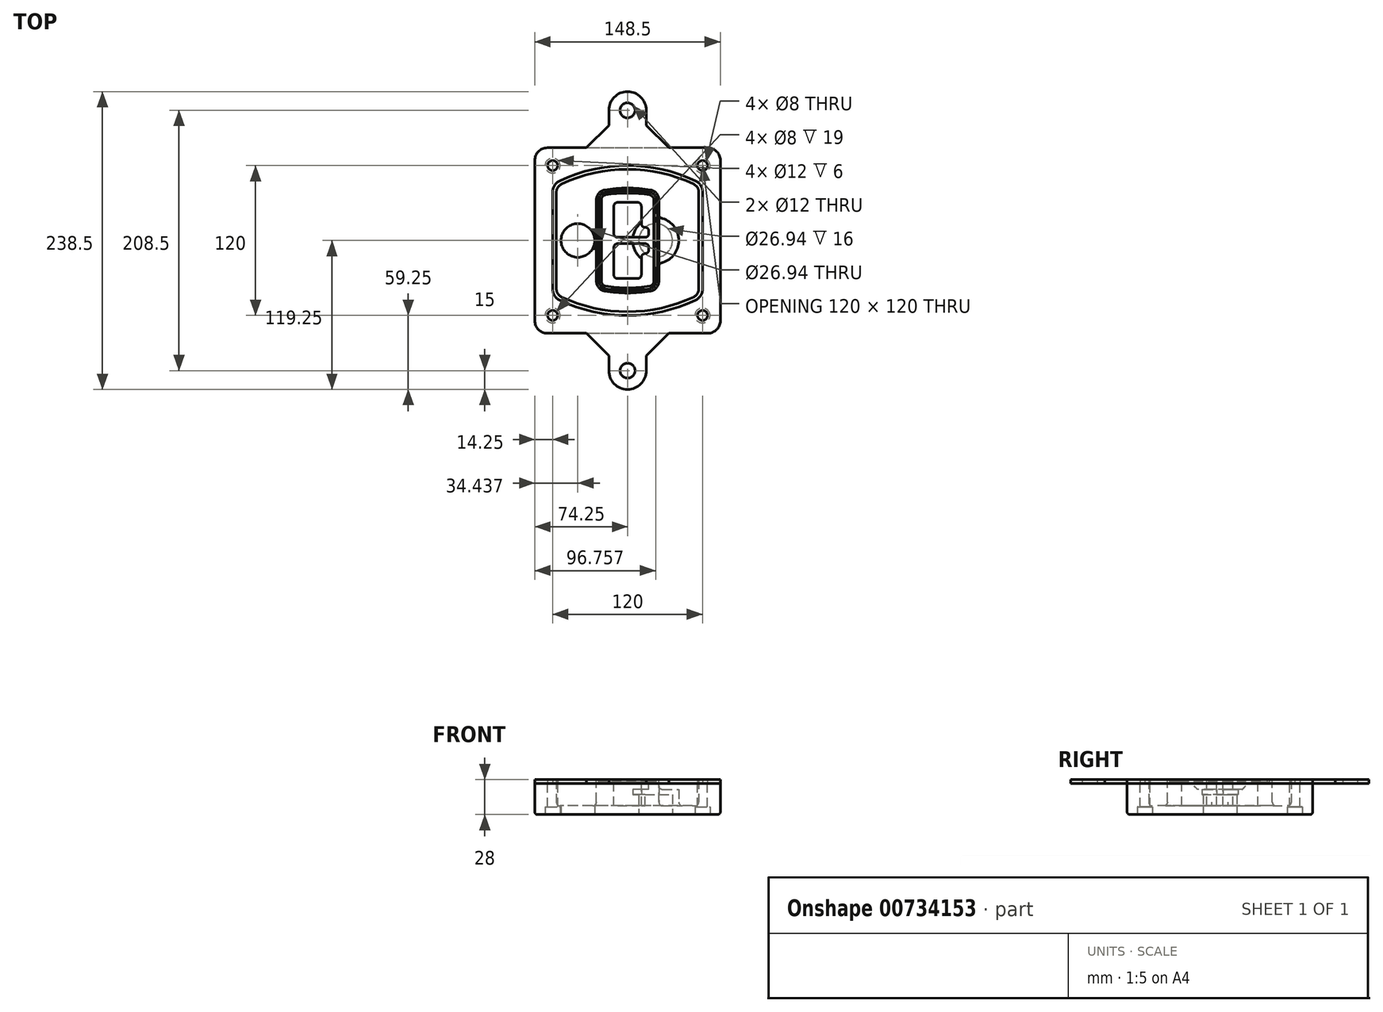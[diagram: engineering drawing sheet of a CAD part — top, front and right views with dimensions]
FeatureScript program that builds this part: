
annotation { "Feature Type Name" : "Feature", "Feature Type Description" : "" }
export const myFeature = defineFeature(function(context is Context, id is Id, definition is map)
    precondition{}
    {
        {
            var Q0;
            Q0=qCreatedBy(makeId("Top.planeOp"),FACE);
            var sketch = newSketch(context, id + "F0", { "sketchPlane" : qUnion([Q0])});
            skPoint(sketch, "E0.rect.middle", {"position": v(0, 0) * mm});
            skLineSegment(sketch, "E1.bottom", {"start": v(-64.25, -74.25) * mm, "end": v(64.25, -74.25) * mm});
            skLineSegment(sketch, "E1.top", {"start": v(-64.25, 74.25) * mm, "end": v(64.25, 74.25) * mm});
            skLineSegment(sketch, "E1.left", {"start": v(-74.25, -64.25) * mm, "end": v(-74.25, 64.25) * mm});
            skLineSegment(sketch, "E1.right", {"start": v(74.25, -64.25) * mm, "end": v(74.25, 64.25) * mm});
            skLineSegment(sketch, "E2", {"start": v(-74.25, 74.25) * mm, "end": v(74.25, -74.25) * mm, "construction": true});
            skLineSegment(sketch, "E3", {"start": v(74.25, 74.25) * mm, "end": v(-74.25, -74.25) * mm, "construction": true});
            skCircle(sketch, "E4", {"center": v(-60, 60) * mm, "radius": 4 * mm});
            skCircle(sketch, "E5", {"center": v(60, 60) * mm, "radius": 4 * mm});
            skCircle(sketch, "E6", {"center": v(60, -60) * mm, "radius": 4 * mm});
            skCircle(sketch, "E7", {"center": v(-60, -60) * mm, "radius": 4 * mm});
            skLineSegment(sketch, "E8", {"start": v(-60, 60) * mm, "end": v(60, 60) * mm, "construction": true});
            skLineSegment(sketch, "E9", {"start": v(60, 60) * mm, "end": v(60, -60) * mm, "construction": true});
            skLineSegment(sketch, "E10", {"start": v(60, -60) * mm, "end": v(-60, -60) * mm, "construction": true});
            skLineSegment(sketch, "E11", {"start": v(-60, -60) * mm, "end": v(-60, 60) * mm, "construction": true});
            skLineSegment(sketch, "E12", {"start": v(-60, 38.83) * mm, "end": v(-60, -38.83) * mm});
            skLineSegment(sketch, "E13", {"start": v(60, 38.83) * mm, "end": v(60, -38.83) * mm});
            skArc(sketch, "E14", {"start": v(54.26, 47.88) * mm, "mid": v(0, 60) * mm, "end": v(-54.26, 47.88) * mm});
            skArc(sketch, "E15", {"start": v(-54.26, -47.88) * mm, "mid": v(0, -60) * mm, "end": v(54.26, -47.88) * mm});
            skLineSegment(sketch, "E16", {"start": v(-60, 0) * mm, "end": v(60, 0) * mm, "construction": true});
            skPoint(sketch, "E17.visualSharp", {"position": v(-60, -45) * mm});
            skArc(sketch, "E17.filletArc", {"start": v(-60, -38.83) * mm, "mid": v(-58.44, -44.2) * mm, "end": v(-54.26, -47.88) * mm});
            skPoint(sketch, "E18.visualSharp", {"position": v(-60, 45) * mm});
            skArc(sketch, "E18.filletArc", {"start": v(-54.26, 47.88) * mm, "mid": v(-58.44, 44.2) * mm, "end": v(-60, 38.83) * mm});
            skPoint(sketch, "E19.visualSharp", {"position": v(60, 45) * mm});
            skArc(sketch, "E19.filletArc", {"start": v(60, 38.83) * mm, "mid": v(58.44, 44.2) * mm, "end": v(54.26, 47.88) * mm});
            skPoint(sketch, "E20.visualSharp", {"position": v(60, -45) * mm});
            skArc(sketch, "E20.filletArc", {"start": v(54.26, -47.88) * mm, "mid": v(58.44, -44.2) * mm, "end": v(60, -38.83) * mm});
            skPoint(sketch, "E21.visualSharp", {"position": v(-74.25, 74.25) * mm});
            skArc(sketch, "E21.filletArc", {"start": v(-64.25, 74.25) * mm, "mid": v(-71.32, 71.32) * mm, "end": v(-74.25, 64.25) * mm});
            skPoint(sketch, "E22.visualSharp", {"position": v(74.25, 74.25) * mm});
            skArc(sketch, "E22.filletArc", {"start": v(74.25, 64.25) * mm, "mid": v(71.32, 71.32) * mm, "end": v(64.25, 74.25) * mm});
            skPoint(sketch, "E23.visualSharp", {"position": v(74.25, -74.25) * mm});
            skArc(sketch, "E23.filletArc", {"start": v(64.25, -74.25) * mm, "mid": v(71.32, -71.32) * mm, "end": v(74.25, -64.25) * mm});
            skPoint(sketch, "E24.visualSharp", {"position": v(-74.25, -74.25) * mm});
            skArc(sketch, "E24.filletArc", {"start": v(-74.25, -64.25) * mm, "mid": v(-71.32, -71.32) * mm, "end": v(-64.25, -74.25) * mm});
            skArc(sketch, "E25.0", {"start": v(57, 38.83) * mm, "mid": v(55.9, 42.58) * mm, "end": v(52.98, 45.17) * mm});
            skLineSegment(sketch, "E25.1", {"start": v(57, 38.83) * mm, "end": v(57, -38.83) * mm});
            skArc(sketch, "E25.2", {"start": v(52.98, -45.17) * mm, "mid": v(55.9, -42.58) * mm, "end": v(57, -38.83) * mm});
            skArc(sketch, "E25.3", {"start": v(-52.98, -45.17) * mm, "mid": v(0, -57) * mm, "end": v(52.98, -45.17) * mm});
            skArc(sketch, "E25.4", {"start": v(-57, -38.83) * mm, "mid": v(-55.9, -42.58) * mm, "end": v(-52.98, -45.17) * mm});
            skArc(sketch, "E25.5", {"start": v(52.98, 45.17) * mm, "mid": v(0, 57) * mm, "end": v(-52.98, 45.17) * mm});
            skLineSegment(sketch, "E25.6", {"start": v(-57, 38.83) * mm, "end": v(-57, -38.83) * mm});
            skArc(sketch, "E25.7", {"start": v(-52.98, 45.17) * mm, "mid": v(-55.9, 42.58) * mm, "end": v(-57, 38.83) * mm});
            skArc(sketch, "E26.0", {"start": v(-55.96, 51.5) * mm, "mid": v(-61.82, 46.33) * mm, "end": v(-64, 38.83) * mm});
            skArc(sketch, "E26.1", {"start": v(55.96, 51.5) * mm, "mid": v(0, 64) * mm, "end": v(-55.96, 51.5) * mm});
            skArc(sketch, "E26.2", {"start": v(64, 38.83) * mm, "mid": v(61.82, 46.33) * mm, "end": v(55.96, 51.5) * mm});
            skLineSegment(sketch, "E26.3", {"start": v(64, 38.83) * mm, "end": v(64, -38.83) * mm});
            skArc(sketch, "E26.4", {"start": v(55.96, -51.5) * mm, "mid": v(61.82, -46.33) * mm, "end": v(64, -38.83) * mm});
            skLineSegment(sketch, "E26.5", {"start": v(-64, 38.83) * mm, "end": v(-64, -38.83) * mm});
            skArc(sketch, "E26.6", {"start": v(-55.96, -51.5) * mm, "mid": v(0, -64) * mm, "end": v(55.96, -51.5) * mm});
            skArc(sketch, "E26.7", {"start": v(-64, -38.83) * mm, "mid": v(-61.82, -46.33) * mm, "end": v(-55.96, -51.5) * mm});
            skSolve(sketch);
        }
        {
            var Q0;
            Q0=makeQuery(id+"F0.imprint","IMPRINT",FACE,{"disambiguationData":[TD([[makeQuery(id+"F0.imprint","IMPRINT",EDGE,{"derivedFrom":sQuery(id+"F0.wireOp",EDGE,"E1.bottom")}),1.0]])]});
            var Q1;
            Q1=makeQuery(id+"F0.imprint","IMPRINT",FACE,{"disambiguationData":[TD([[makeQuery(id+"F0.imprint","IMPRINT",EDGE,{"derivedFrom":sQuery(id+"F0.wireOp",EDGE,"E12")}),1.0]])]});
            var Q2;
            Q2=makeQuery(id+"F0.imprint","IMPRINT",FACE,{"disambiguationData":[TD([[makeQuery(id+"F0.imprint","IMPRINT",EDGE,{"derivedFrom":sQuery(id+"F0.wireOp",EDGE,"E25.0")}),1.0]])]});
            var Q3;
            Q3=makeQuery(id+"F0.imprint","IMPRINT",FACE,{"disambiguationData":[TD([[makeQuery(id+"F0.imprint","IMPRINT",EDGE,{"derivedFrom":sQuery(id+"F0.wireOp",EDGE,"E12")}),-1.0]])]});
            extrude(context, id + "F1", {"entities" : qUnion([Q0, Q1, Q2, Q3]), "oppositeDirection" : true, "depth" : 25 * mm});
        }
        {
            var Q0;
            Q0=makeQuery(id+"F0.imprint","IMPRINT",FACE,{"disambiguationData":[TD([[makeQuery(id+"F0.imprint","IMPRINT",EDGE,{"derivedFrom":sQuery(id+"F0.wireOp",EDGE,"E12")}),1.0]])]});
            extrude(context, id + "F2", {"entities" : qUnion([Q0]), "operationType" : NewBodyOperationType.ADD, "depth" : 3 * mm});
        }
        {
            var Q0;
            Q0=makeQuery(id+"F0.imprint","IMPRINT",FACE,{"disambiguationData":[TD([[makeQuery(id+"F0.imprint","IMPRINT",EDGE,{"derivedFrom":sQuery(id+"F0.wireOp",EDGE,"E25.0")}),1.0]])]});
            extrude(context, id + "F3", {"entities" : qUnion([Q0]), "operationType" : NewBodyOperationType.REMOVE, "oppositeDirection" : true, "depth" : 18 * mm});
        }
        {
            var Q0;
            Q0=makeQuery(id+"F2.opExtrude","CAP_FACE",FACE,{"disambiguationData":[OSD([sQuery(id+"F0.wireOp",EDGE,"E12"),sQuery(id+"F0.wireOp",EDGE,"E13"),sQuery(id+"F0.wireOp",EDGE,"E14"),sQuery(id+"F0.wireOp",EDGE,"E15"),sQuery(id+"F0.wireOp",EDGE,"E17.filletArc"),sQuery(id+"F0.wireOp",EDGE,"E18.filletArc"),sQuery(id+"F0.wireOp",EDGE,"E19.filletArc"),sQuery(id+"F0.wireOp",EDGE,"E20.filletArc"),sQuery(id+"F0.wireOp",EDGE,"E25.0"),sQuery(id+"F0.wireOp",EDGE,"E25.1"),sQuery(id+"F0.wireOp",EDGE,"E25.2"),sQuery(id+"F0.wireOp",EDGE,"E25.3"),sQuery(id+"F0.wireOp",EDGE,"E25.4"),sQuery(id+"F0.wireOp",EDGE,"E25.5"),sQuery(id+"F0.wireOp",EDGE,"E25.6"),sQuery(id+"F0.wireOp",EDGE,"E25.7")])],"isStart":false});
            var sketch = newSketch(context, id + "F4", { "sketchPlane" : qUnion([Q0])});
            skArc(sketch, "E27.0", {"start": v(-18.34, -40.45) * mm, "mid": v(0, -42) * mm, "end": v(18.34, -40.45) * mm});
            skArc(sketch, "E28.0", {"start": v(18.34, 40.45) * mm, "mid": v(0, 42) * mm, "end": v(-18.34, 40.45) * mm});
            skLineSegment(sketch, "E29", {"start": v(-25, 32.57) * mm, "end": v(-25, -32.57) * mm});
            skLineSegment(sketch, "E30", {"start": v(25, 32.57) * mm, "end": v(25, -32.57) * mm});
            skLineSegment(sketch, "E31", {"start": v(-25, 39.1) * mm, "end": v(25, 39.1) * mm, "construction": true});
            skLineSegment(sketch, "E32", {"start": v(-25, -39.1) * mm, "end": v(25, -39.1) * mm, "construction": true});
            skPoint(sketch, "E33.visualSharp", {"position": v(-25, 39.1) * mm});
            skArc(sketch, "E33.filletArc", {"start": v(-18.34, 40.45) * mm, "mid": v(-23.11, 37.73) * mm, "end": v(-25, 32.57) * mm});
            skPoint(sketch, "E34.visualSharp", {"position": v(25, 39.1) * mm});
            skArc(sketch, "E34.filletArc", {"start": v(25, 32.57) * mm, "mid": v(23.11, 37.73) * mm, "end": v(18.34, 40.45) * mm});
            skPoint(sketch, "E35.visualSharp", {"position": v(25, -39.1) * mm});
            skArc(sketch, "E35.filletArc", {"start": v(18.34, -40.45) * mm, "mid": v(23.11, -37.73) * mm, "end": v(25, -32.57) * mm});
            skPoint(sketch, "E36.visualSharp", {"position": v(-25, -39.1) * mm});
            skArc(sketch, "E36.filletArc", {"start": v(-25, -32.57) * mm, "mid": v(-23.11, -37.73) * mm, "end": v(-18.34, -40.45) * mm});
            skArc(sketch, "E37.0", {"start": v(52.98, 45.17) * mm, "mid": v(0, 57) * mm, "end": v(-52.98, 45.17) * mm});
            skArc(sketch, "E37.1", {"start": v(-52.98, 45.17) * mm, "mid": v(-55.9, 42.58) * mm, "end": v(-57, 38.83) * mm});
            skLineSegment(sketch, "E37.2", {"start": v(-57, 38.83) * mm, "end": v(-57, -38.83) * mm});
            skArc(sketch, "E37.3", {"start": v(-57, -38.83) * mm, "mid": v(-55.9, -42.58) * mm, "end": v(-52.98, -45.17) * mm});
            skArc(sketch, "E37.4", {"start": v(-52.98, -45.17) * mm, "mid": v(0, -57) * mm, "end": v(52.98, -45.17) * mm});
            skArc(sketch, "E37.5", {"start": v(52.98, -45.17) * mm, "mid": v(55.9, -42.58) * mm, "end": v(57, -38.83) * mm});
            skLineSegment(sketch, "E37.6", {"start": v(57, 38.83) * mm, "end": v(57, -38.83) * mm});
            skArc(sketch, "E37.7", {"start": v(57, 38.83) * mm, "mid": v(55.9, 42.58) * mm, "end": v(52.98, 45.17) * mm});
            skLineSegment(sketch, "E38.0", {"start": v(23, 32.57) * mm, "end": v(23, -32.57) * mm});
            skArc(sketch, "E38.1", {"start": v(18, -38.48) * mm, "mid": v(21.58, -36.44) * mm, "end": v(23, -32.57) * mm});
            skArc(sketch, "E38.2", {"start": v(-18, -38.48) * mm, "mid": v(0, -40) * mm, "end": v(18, -38.48) * mm});
            skArc(sketch, "E38.3", {"start": v(-23, -32.57) * mm, "mid": v(-21.58, -36.44) * mm, "end": v(-18, -38.48) * mm});
            skLineSegment(sketch, "E38.4", {"start": v(-23, 32.57) * mm, "end": v(-23, -32.57) * mm});
            skArc(sketch, "E38.5", {"start": v(23, 32.57) * mm, "mid": v(21.58, 36.44) * mm, "end": v(18, 38.48) * mm});
            skArc(sketch, "E38.6", {"start": v(-18, 38.48) * mm, "mid": v(-21.58, 36.44) * mm, "end": v(-23, 32.57) * mm});
            skArc(sketch, "E38.7", {"start": v(18, 38.48) * mm, "mid": v(0, 40) * mm, "end": v(-18, 38.48) * mm});
            skArc(sketch, "E39.0", {"start": v(21, 32.57) * mm, "mid": v(20.06, 35.15) * mm, "end": v(17.67, 36.5) * mm});
            skLineSegment(sketch, "E39.1", {"start": v(21, 32.57) * mm, "end": v(21, -32.57) * mm});
            skArc(sketch, "E39.2", {"start": v(17.67, -36.5) * mm, "mid": v(20.06, -35.15) * mm, "end": v(21, -32.57) * mm});
            skArc(sketch, "E39.3", {"start": v(-17.67, -36.5) * mm, "mid": v(0, -38) * mm, "end": v(17.67, -36.5) * mm});
            skArc(sketch, "E39.4", {"start": v(-21, -32.57) * mm, "mid": v(-20.06, -35.15) * mm, "end": v(-17.67, -36.5) * mm});
            skArc(sketch, "E39.5", {"start": v(17.67, 36.5) * mm, "mid": v(0, 38) * mm, "end": v(-17.67, 36.5) * mm});
            skLineSegment(sketch, "E39.6", {"start": v(-21, 32.57) * mm, "end": v(-21, -32.57) * mm});
            skArc(sketch, "E39.7", {"start": v(-17.67, 36.5) * mm, "mid": v(-20.06, 35.15) * mm, "end": v(-21, 32.57) * mm});
            skLineSegment(sketch, "E40", {"start": v(-25, 0) * mm, "end": v(25, 0) * mm, "construction": true});
            skLineSegment(sketch, "E41", {"start": v(-11, 5.5) * mm, "end": v(-11, 27.5) * mm});
            skLineSegment(sketch, "E42", {"start": v(-8, 30.5) * mm, "end": v(8, 30.5) * mm});
            skLineSegment(sketch, "E43", {"start": v(11, 27.5) * mm, "end": v(11, 13.5) * mm});
            skLineSegment(sketch, "E44", {"start": v(14, 10.5) * mm, "end": v(14, 10.5) * mm});
            skLineSegment(sketch, "E45", {"start": v(17, 7.5) * mm, "end": v(17, 5.5) * mm});
            skLineSegment(sketch, "E46", {"start": v(14, 2.5) * mm, "end": v(-8, 2.5) * mm});
            skPoint(sketch, "E47.visualSharp", {"position": v(-11, 30.5) * mm});
            skArc(sketch, "E47.filletArc", {"start": v(-8, 30.5) * mm, "mid": v(-10.12, 29.62) * mm, "end": v(-11, 27.5) * mm});
            skPoint(sketch, "E48.visualSharp", {"position": v(11, 30.5) * mm});
            skArc(sketch, "E48.filletArc", {"start": v(11, 27.5) * mm, "mid": v(10.12, 29.62) * mm, "end": v(8, 30.5) * mm});
            skPoint(sketch, "E49.visualSharp", {"position": v(11, 10.5) * mm});
            skArc(sketch, "E49.filletArc", {"start": v(11, 13.5) * mm, "mid": v(11.88, 11.38) * mm, "end": v(14, 10.5) * mm});
            skPoint(sketch, "E50.visualSharp", {"position": v(17, 10.5) * mm});
            skArc(sketch, "E50.filletArc", {"start": v(17, 7.5) * mm, "mid": v(16.12, 9.62) * mm, "end": v(14, 10.5) * mm});
            skPoint(sketch, "E51.visualSharp", {"position": v(17, 2.5) * mm});
            skArc(sketch, "E51.filletArc", {"start": v(14, 2.5) * mm, "mid": v(16.12, 3.38) * mm, "end": v(17, 5.5) * mm});
            skPoint(sketch, "E52.visualSharp", {"position": v(-11, 2.5) * mm});
            skArc(sketch, "E52.filletArc", {"start": v(-11, 5.5) * mm, "mid": v(-10.12, 3.38) * mm, "end": v(-8, 2.5) * mm});
            skLineSegment(sketch, "E53.0.MirrorCS", {"start": v(14, -2.5) * mm, "end": v(-8, -2.5) * mm});
            skArc(sketch, "E54.0.MirrorCS", {"start": v(-11, -5.5) * mm, "mid": v(-10.12, -3.38) * mm, "end": v(-8, -2.5) * mm});
            skLineSegment(sketch, "E55.0.MirrorCS", {"start": v(-11, -5.5) * mm, "end": v(-11, -27.5) * mm});
            skArc(sketch, "E56.0.MirrorCS", {"start": v(-8, -30.5) * mm, "mid": v(-10.12, -29.62) * mm, "end": v(-11, -27.5) * mm});
            skLineSegment(sketch, "E57.0.MirrorCS", {"start": v(-8, -30.5) * mm, "end": v(8, -30.5) * mm});
            skArc(sketch, "E58.0.MirrorCS", {"start": v(11, -27.5) * mm, "mid": v(10.12, -29.62) * mm, "end": v(8, -30.5) * mm});
            skLineSegment(sketch, "E59.0.MirrorCS", {"start": v(11, -27.5) * mm, "end": v(11, -13.5) * mm});
            skArc(sketch, "E60.0.MirrorCS", {"start": v(11, -13.5) * mm, "mid": v(11.88, -11.38) * mm, "end": v(14, -10.5) * mm});
            skArc(sketch, "E61.0.MirrorCS", {"start": v(17, -7.5) * mm, "mid": v(16.12, -9.62) * mm, "end": v(14, -10.5) * mm});
            skLineSegment(sketch, "E62.0.MirrorCS", {"start": v(17, -7.5) * mm, "end": v(17, -5.5) * mm});
            skArc(sketch, "E63.0.MirrorCS", {"start": v(14, -2.5) * mm, "mid": v(16.12, -3.38) * mm, "end": v(17, -5.5) * mm});
            skSolve(sketch);
        }
        {
            var Q0;
            Q0=makeQuery(id+"F4.imprint","IMPRINT",FACE,{"disambiguationData":[TD([[makeQuery(id+"F4.imprint","IMPRINT",EDGE,{"derivedFrom":sQuery(id+"F4.wireOp",EDGE,"E27.0")}),1.0]])]});
            var Q1;
            Q1=makeQuery(id+"F4.imprint","IMPRINT",FACE,{"disambiguationData":[TD([[makeQuery(id+"F4.imprint","IMPRINT",EDGE,{"derivedFrom":sQuery(id+"F4.wireOp",EDGE,"E38.0")}),-1.0]])]});
            var Q2;
            Q2=makeQuery(id+"F4.imprint","IMPRINT",FACE,{"disambiguationData":[TD([[makeQuery(id+"F4.imprint","IMPRINT",EDGE,{"derivedFrom":sQuery(id+"F4.wireOp",EDGE,"E39.0")}),1.0]])]});
            extrude(context, id + "F5", {"entities" : qUnion([Q0, Q1, Q2]), "operationType" : NewBodyOperationType.ADD, "endBound" : BoundingType.UP_TO_NEXT, "oppositeDirection" : true, "depth" : 25 * mm});
        }
        {
            var Q0;
            Q0=makeQuery(id+"F4.imprint","IMPRINT",FACE,{"disambiguationData":[TD([[makeQuery(id+"F4.imprint","IMPRINT",EDGE,{"derivedFrom":sQuery(id+"F4.wireOp",EDGE,"E38.0")}),-1.0]])]});
            extrude(context, id + "F6", {"entities" : qUnion([Q0]), "operationType" : NewBodyOperationType.REMOVE, "oppositeDirection" : true, "depth" : 2 * mm});
        }
        {
            var Q0;
            Q0=makeQuery(id+"F1.opExtrude","CAP_FACE",FACE,{"disambiguationData":[OSD([sQuery(id+"F0.wireOp",EDGE,"E1.bottom"),sQuery(id+"F0.wireOp",EDGE,"E1.top"),sQuery(id+"F0.wireOp",EDGE,"E1.left"),sQuery(id+"F0.wireOp",EDGE,"E1.right"),sQuery(id+"F0.wireOp",EDGE,"E4"),sQuery(id+"F0.wireOp",EDGE,"E5"),sQuery(id+"F0.wireOp",EDGE,"E6"),sQuery(id+"F0.wireOp",EDGE,"E7"),sQuery(id+"F0.wireOp",EDGE,"E21.filletArc"),sQuery(id+"F0.wireOp",EDGE,"E22.filletArc"),sQuery(id+"F0.wireOp",EDGE,"E23.filletArc"),sQuery(id+"F0.wireOp",EDGE,"E24.filletArc")])],"isStart":false});
            var sketch = newSketch(context, id + "F7", { "sketchPlane" : qUnion([Q0])});
            skCircle(sketch, "E64", {"center": v(22.5, 0) * mm, "radius": 13.47 * mm});
            skCircle(sketch, "E65", {"center": v(-39.81, 0) * mm, "radius": 13.47 * mm});
            skLineSegment(sketch, "E66", {"start": v(74.25, 0) * mm, "end": v(-74.25, 0) * mm});
            skCircle(sketch, "E67", {"center": v(22.5, 0) * mm, "radius": 18.47 * mm});
            skCircle(sketch, "E68", {"center": v(60, -60) * mm, "radius": 6 * mm});
            skCircle(sketch, "E69", {"center": v(-60, -60) * mm, "radius": 6 * mm});
            skCircle(sketch, "E70", {"center": v(-60, 60) * mm, "radius": 6 * mm});
            skCircle(sketch, "E71", {"center": v(60, 60) * mm, "radius": 6 * mm});
            skSolve(sketch);
        }
        {
            var Q0;
            {var subQ1=sQuery(id+"F7.wireOp",EDGE,"E66");var subQ4=sQuery(id+"F7.wireOp",EDGE,"E64");var subQ6=makeQuery(id+"F7.imprint","INTERSECT",VERTEX,{"disambiguationData":[OD(0.0)],"derivedFrom":[subQ4,subQ1]});Q0=makeQuery(id+"F7.imprint","IMPRINT",FACE,{"disambiguationData":[TD([[makeQuery(id+"F7.imprint","IMPRINT",EDGE,{"disambiguationData":[TD([[subQ6,-1.0]])],"derivedFrom":subQ4}),-1.0]])]});}
            var Q1;
            {var subQ0=sQuery(id+"F7.wireOp",EDGE,"E66");var subQ1=sQuery(id+"F7.wireOp",EDGE,"E64");var subQ3=makeQuery(id+"F7.imprint","INTERSECT",VERTEX,{"disambiguationData":[OD(0.0)],"derivedFrom":[subQ1,subQ0]});Q1=makeQuery(id+"F7.imprint","IMPRINT",FACE,{"disambiguationData":[TD([[makeQuery(id+"F7.imprint","IMPRINT",EDGE,{"disambiguationData":[TD([[subQ3,-1.0]])],"derivedFrom":subQ1}),1.0]])]});}
            var Q2;
            {var subQ0=sQuery(id+"F7.wireOp",EDGE,"E66");var subQ1=sQuery(id+"F7.wireOp",EDGE,"E64");var subQ3=makeQuery(id+"F7.imprint","INTERSECT",VERTEX,{"disambiguationData":[OD(0.0)],"derivedFrom":[subQ1,subQ0]});Q2=makeQuery(id+"F7.imprint","IMPRINT",FACE,{"disambiguationData":[TD([[makeQuery(id+"F7.imprint","IMPRINT",EDGE,{"disambiguationData":[TD([[subQ3,1.0]])],"derivedFrom":subQ1}),1.0]])]});}
            var Q3;
            {var subQ1=sQuery(id+"F7.wireOp",EDGE,"E66");var subQ4=sQuery(id+"F7.wireOp",EDGE,"E64");var subQ6=makeQuery(id+"F7.imprint","INTERSECT",VERTEX,{"disambiguationData":[OD(0.0)],"derivedFrom":[subQ4,subQ1]});Q3=makeQuery(id+"F7.imprint","IMPRINT",FACE,{"disambiguationData":[TD([[makeQuery(id+"F7.imprint","IMPRINT",EDGE,{"disambiguationData":[TD([[subQ6,1.0]])],"derivedFrom":subQ4}),-1.0]])]});}
            extrude(context, id + "F8", {"entities" : qUnion([Q0, Q1, Q2, Q3]), "operationType" : NewBodyOperationType.ADD, "oppositeDirection" : true, "depth" : 20 * mm});
        }
        {
            var Q0;
            {var subQ0=sQuery(id+"F7.wireOp",EDGE,"E66");var subQ1=sQuery(id+"F7.wireOp",EDGE,"E64");var subQ3=makeQuery(id+"F7.imprint","INTERSECT",VERTEX,{"disambiguationData":[OD(0.0)],"derivedFrom":[subQ1,subQ0]});Q0=makeQuery(id+"F7.imprint","IMPRINT",FACE,{"disambiguationData":[TD([[makeQuery(id+"F7.imprint","IMPRINT",EDGE,{"disambiguationData":[TD([[subQ3,-1.0]])],"derivedFrom":subQ1}),1.0]])]});}
            var Q1;
            {var subQ0=sQuery(id+"F7.wireOp",EDGE,"E66");var subQ1=sQuery(id+"F7.wireOp",EDGE,"E64");var subQ3=makeQuery(id+"F7.imprint","INTERSECT",VERTEX,{"disambiguationData":[OD(0.0)],"derivedFrom":[subQ1,subQ0]});Q1=makeQuery(id+"F7.imprint","IMPRINT",FACE,{"disambiguationData":[TD([[makeQuery(id+"F7.imprint","IMPRINT",EDGE,{"disambiguationData":[TD([[subQ3,1.0]])],"derivedFrom":subQ1}),1.0]])]});}
            extrude(context, id + "F9", {"entities" : qUnion([Q0, Q1]), "operationType" : NewBodyOperationType.REMOVE, "oppositeDirection" : true, "depth" : 16 * mm});
        }
        {
            var Q0;
            {var subQ0=sQuery(id+"F7.wireOp",EDGE,"E66");var subQ1=sQuery(id+"F7.wireOp",EDGE,"E65");var subQ3=makeQuery(id+"F7.imprint","INTERSECT",VERTEX,{"disambiguationData":[OD(0.0)],"derivedFrom":[subQ1,subQ0]});Q0=makeQuery(id+"F7.imprint","IMPRINT",FACE,{"disambiguationData":[TD([[makeQuery(id+"F7.imprint","IMPRINT",EDGE,{"disambiguationData":[TD([[subQ3,-1.0]])],"derivedFrom":subQ1}),1.0]])]});}
            var Q1;
            {var subQ0=sQuery(id+"F7.wireOp",EDGE,"E66");var subQ1=sQuery(id+"F7.wireOp",EDGE,"E65");var subQ3=makeQuery(id+"F7.imprint","INTERSECT",VERTEX,{"disambiguationData":[OD(0.0)],"derivedFrom":[subQ1,subQ0]});Q1=makeQuery(id+"F7.imprint","IMPRINT",FACE,{"disambiguationData":[TD([[makeQuery(id+"F7.imprint","IMPRINT",EDGE,{"disambiguationData":[TD([[subQ3,1.0]])],"derivedFrom":subQ1}),1.0]])]});}
            extrude(context, id + "F10", {"entities" : qUnion([Q0, Q1]), "operationType" : NewBodyOperationType.REMOVE, "oppositeDirection" : true, "depth" : 25 * mm});
        }
        {
            var Q0;
            Q0=makeQuery(id+"F7.imprint","IMPRINT",FACE,{"disambiguationData":[TD([[makeQuery(id+"F7.imprint","IMPRINT",EDGE,{"derivedFrom":sQuery(id+"F7.wireOp",EDGE,"E68")}),1.0]])]});
            var Q1;
            Q1=makeQuery(id+"F7.imprint","IMPRINT",FACE,{"disambiguationData":[TD([[makeQuery(id+"F7.imprint","IMPRINT",EDGE,{"derivedFrom":makeQuery(id+"F1.opExtrude","CAP_EDGE",EDGE,{"disambiguationData":[OSD([sQuery(id+"F0.wireOp",EDGE,"E5")])],"isStart":false})}),-1.0]])]});
            var Q2;
            Q2=makeQuery(id+"F7.imprint","IMPRINT",FACE,{"disambiguationData":[TD([[makeQuery(id+"F7.imprint","IMPRINT",EDGE,{"derivedFrom":sQuery(id+"F7.wireOp",EDGE,"E69")}),1.0]])]});
            var Q3;
            Q3=makeQuery(id+"F7.imprint","IMPRINT",FACE,{"disambiguationData":[TD([[makeQuery(id+"F7.imprint","IMPRINT",EDGE,{"derivedFrom":makeQuery(id+"F1.opExtrude","CAP_EDGE",EDGE,{"disambiguationData":[OSD([sQuery(id+"F0.wireOp",EDGE,"E4")])],"isStart":false})}),-1.0]])]});
            var Q4;
            Q4=makeQuery(id+"F7.imprint","IMPRINT",FACE,{"disambiguationData":[TD([[makeQuery(id+"F7.imprint","IMPRINT",EDGE,{"derivedFrom":sQuery(id+"F7.wireOp",EDGE,"E70")}),1.0]])]});
            var Q5;
            Q5=makeQuery(id+"F7.imprint","IMPRINT",FACE,{"disambiguationData":[TD([[makeQuery(id+"F7.imprint","IMPRINT",EDGE,{"derivedFrom":makeQuery(id+"F1.opExtrude","CAP_EDGE",EDGE,{"disambiguationData":[OSD([sQuery(id+"F0.wireOp",EDGE,"E7")])],"isStart":false})}),-1.0]])]});
            var Q6;
            Q6=makeQuery(id+"F7.imprint","IMPRINT",FACE,{"disambiguationData":[TD([[makeQuery(id+"F7.imprint","IMPRINT",EDGE,{"derivedFrom":sQuery(id+"F7.wireOp",EDGE,"E71")}),1.0]])]});
            var Q7;
            Q7=makeQuery(id+"F7.imprint","IMPRINT",FACE,{"disambiguationData":[TD([[makeQuery(id+"F7.imprint","IMPRINT",EDGE,{"derivedFrom":makeQuery(id+"F1.opExtrude","CAP_EDGE",EDGE,{"disambiguationData":[OSD([sQuery(id+"F0.wireOp",EDGE,"E6")])],"isStart":false})}),-1.0]])]});
            extrude(context, id + "F11", {"entities" : qUnion([Q0, Q1, Q2, Q3, Q4, Q5, Q6, Q7]), "operationType" : NewBodyOperationType.REMOVE, "oppositeDirection" : true, "depth" : 6 * mm});
        }
        {
            var Q0;
            Q0=makeQuery(id+"F9.boolean.opBoolean","COPY",FACE,{"derivedFrom":makeQuery(id+"F9.opExtrude","CAP_FACE",FACE,{"disambiguationData":[OSD([sQuery(id+"F7.wireOp",EDGE,"E64")])],"isStart":false})});
            var sketch = newSketch(context, id + "F12", { "sketchPlane" : qUnion([Q0])});
            skArc(sketch, "E72.0", {"start": v(11, 14.45) * mm, "mid": v(6.45, 9.13) * mm, "end": v(4.2, 2.5) * mm});
            skArc(sketch, "E72.1", {"start": v(4.2, -2.5) * mm, "mid": v(6.45, -9.13) * mm, "end": v(11, -14.45) * mm});
            skLineSegment(sketch, "E73", {"start": v(4.2, -2.5) * mm, "end": v(14, -2.5) * mm});
            skLineSegment(sketch, "E74.0", {"start": v(14, 2.5) * mm, "end": v(4.2, 2.5) * mm});
            skArc(sketch, "E74.1", {"start": v(14, 2.5) * mm, "mid": v(16.12, 3.38) * mm, "end": v(17, 5.5) * mm});
            skLineSegment(sketch, "E74.2", {"start": v(17, 7.5) * mm, "end": v(17, 5.5) * mm});
            skArc(sketch, "E74.3", {"start": v(17, 7.5) * mm, "mid": v(16.12, 9.62) * mm, "end": v(14, 10.5) * mm});
            skArc(sketch, "E74.4", {"start": v(11, 13.5) * mm, "mid": v(11.88, 11.38) * mm, "end": v(14, 10.5) * mm});
            skLineSegment(sketch, "E74.5", {"start": v(11, 14.45) * mm, "end": v(11, 13.5) * mm});
            skLineSegment(sketch, "E74.7", {"start": v(14, -2.5) * mm, "end": v(4.2, -2.5) * mm});
            skArc(sketch, "E74.8", {"start": v(14, -2.5) * mm, "mid": v(16.12, -3.38) * mm, "end": v(17, -5.5) * mm});
            skLineSegment(sketch, "E74.9", {"start": v(17, -7.5) * mm, "end": v(17, -5.5) * mm});
            skArc(sketch, "E74.10", {"start": v(17, -7.5) * mm, "mid": v(16.12, -9.62) * mm, "end": v(14, -10.5) * mm});
            skArc(sketch, "E74.11", {"start": v(11, -13.5) * mm, "mid": v(11.88, -11.38) * mm, "end": v(14, -10.5) * mm});
            skLineSegment(sketch, "E74.12", {"start": v(11, -14.45) * mm, "end": v(11, -13.5) * mm});
            skPoint(sketch, "E75.orphan", {"position": v(11, -27.5) * mm});
            skPoint(sketch, "E76.orphan", {"position": v(-8, -2.5) * mm});
            skPoint(sketch, "E77.orphan", {"position": v(-8, 2.5) * mm});
            skPoint(sketch, "E78.orphan", {"position": v(11, 27.5) * mm});
            skSolve(sketch);
        }
        {
            var Q0;
            {var subQ7=sQuery(id+"F12.wireOp",EDGE,"E72.0");var subQ14=sQuery(id+"F12.wireOp",EDGE,"E72.1");var subQ16=sQuery(id+"F12.wireOp",EDGE,"E74.1");var subQ18=sQuery(id+"F12.wireOp",EDGE,"E74.8");Q0=qUnion([makeQuery(id+"F12.imprint","IMPRINT",FACE,{"disambiguationData":[TD([[makeQuery(id+"F12.imprint","IMPRINT",EDGE,{"derivedFrom":subQ7}),1.0]])]}),makeQuery(id+"F12.imprint","IMPRINT",FACE,{"disambiguationData":[TD([[makeQuery(id+"F12.imprint","IMPRINT",EDGE,{"derivedFrom":subQ14}),1.0]])]}),makeQuery(id+"F12.imprint","IMPRINT",FACE,{"disambiguationData":[TD([[makeQuery(id+"F12.imprint","IMPRINT",EDGE,{"derivedFrom":subQ16}),1.0]])]}),makeQuery(id+"F12.imprint","IMPRINT",FACE,{"disambiguationData":[TD([[makeQuery(id+"F12.imprint","IMPRINT",EDGE,{"derivedFrom":subQ18}),-1.0]])]})]);}
            var Q1;
            Q1=makeQuery(id+"F5.boolean.opBoolean","SPLIT",FACE,{"disambiguationData":[TD([makeQuery(id+"F5.opExtrude","SWEPT_FACE",FACE,{"disambiguationData":[OSD([sQuery(id+"F4.wireOp",EDGE,"E41")])]})])],"derivedFrom":makeQuery(id+"F3.boolean.opBoolean","COPY",FACE,{"derivedFrom":makeQuery(id+"F3.opExtrude","CAP_FACE",FACE,{"disambiguationData":[OSD([sQuery(id+"F0.wireOp",EDGE,"E25.0"),sQuery(id+"F0.wireOp",EDGE,"E25.1"),sQuery(id+"F0.wireOp",EDGE,"E25.2"),sQuery(id+"F0.wireOp",EDGE,"E25.3"),sQuery(id+"F0.wireOp",EDGE,"E25.4"),sQuery(id+"F0.wireOp",EDGE,"E25.5"),sQuery(id+"F0.wireOp",EDGE,"E25.6"),sQuery(id+"F0.wireOp",EDGE,"E25.7")])],"isStart":false})})});
            extrude(context, id + "F13", {"entities" : qUnion([Q0]), "operationType" : NewBodyOperationType.REMOVE, "endBound" : BoundingType.UP_TO_SURFACE, "endBoundEntityFace" : qUnion([Q1]), "depth" : 25 * mm});
        }
        {
            var Q0;
            Q0=makeQuery(id+"F3.boolean.opBoolean","COPY",EDGE,{"derivedFrom":makeQuery(id+"F3.opExtrude","CAP_EDGE",EDGE,{"disambiguationData":[OSD([sQuery(id+"F0.wireOp",EDGE,"E25.6")])],"isStart":false})});
            var Q1;
            Q1=makeQuery(id+"F8.boolean.opBoolean","INTERSECT",EDGE,{"derivedFrom":[makeQuery(id+"F5.opExtrude","SWEPT_FACE",FACE,{"disambiguationData":[OSD([sQuery(id+"F4.wireOp",EDGE,"E30")])]}),makeQuery(id+"F8.opExtrude","CAP_FACE",FACE,{"disambiguationData":[OSD([sQuery(id+"F7.wireOp",EDGE,"E67")])],"isStart":false})]});
            var Q2;
            Q2=makeQuery(id+"F8.boolean.opBoolean","INTERSECT",EDGE,{"disambiguationData":[OD(1.0)],"derivedFrom":[makeQuery(id+"F5.opExtrude","SWEPT_FACE",FACE,{"disambiguationData":[OSD([sQuery(id+"F4.wireOp",EDGE,"E30")])]}),makeQuery(id+"F8.opExtrude","SWEPT_FACE",FACE,{"disambiguationData":[OSD([sQuery(id+"F7.wireOp",EDGE,"E67")])]})]});
            var Q3;
            {var subQ0=sQuery(id+"F4.wireOp",EDGE,"E30");Q3=makeQuery(id+"F8.boolean.opBoolean","SPLIT",EDGE,{"disambiguationData":[TD([makeQuery(id+"F5.opExtrude","SWEPT_FACE",FACE,{"disambiguationData":[OSD([sQuery(id+"F4.wireOp",EDGE,"E35.filletArc")])]})])],"derivedFrom":makeQuery(id+"F5.opExtrude","CAP_EDGE",EDGE,{"disambiguationData":[OSD([subQ0])],"isStart":false})});}
            var Q4;
            {var subQ0=sQuery(id+"F0.wireOp",EDGE,"E25.7");var subQ1=sQuery(id+"F0.wireOp",EDGE,"E25.1");var subQ2=sQuery(id+"F0.wireOp",EDGE,"E25.6");var subQ3=sQuery(id+"F0.wireOp",EDGE,"E25.5");var subQ4=sQuery(id+"F0.wireOp",EDGE,"E25.4");var subQ5=sQuery(id+"F0.wireOp",EDGE,"E25.0");var subQ6=sQuery(id+"F0.wireOp",EDGE,"E25.2");var subQ7=sQuery(id+"F0.wireOp",EDGE,"E25.3");Q4=makeQuery(id+"F8.boolean.opBoolean","INTERSECT",EDGE,{"derivedFrom":[makeQuery(id+"F5.boolean.opBoolean","SPLIT",FACE,{"disambiguationData":[TD([makeQuery(id+"F2.opExtrude","SWEPT_FACE",FACE,{"disambiguationData":[OSD([subQ5])]})])],"derivedFrom":makeQuery(id+"F3.boolean.opBoolean","COPY",FACE,{"derivedFrom":makeQuery(id+"F3.opExtrude","CAP_FACE",FACE,{"disambiguationData":[OSD([subQ5,subQ1,subQ6,subQ7,subQ4,subQ3,subQ2,subQ0])],"isStart":false})})}),makeQuery(id+"F8.opExtrude","SWEPT_FACE",FACE,{"disambiguationData":[OSD([sQuery(id+"F7.wireOp",EDGE,"E67")])]})]});}
            var Q5;
            Q5=makeQuery(id+"F8.boolean.opBoolean","INTERSECT",EDGE,{"disambiguationData":[OD(0.0)],"derivedFrom":[makeQuery(id+"F5.opExtrude","SWEPT_FACE",FACE,{"disambiguationData":[OSD([sQuery(id+"F4.wireOp",EDGE,"E30")])]}),makeQuery(id+"F8.opExtrude","SWEPT_FACE",FACE,{"disambiguationData":[OSD([sQuery(id+"F7.wireOp",EDGE,"E67")])]})]});
            fillet(context, id + "F14", {"entities" : qUnion([Q0, Q1, Q2, Q3, Q4, Q5]), "radius" : 3 * mm, "tangentPropagation" : true, "allowEdgeOverflow" : false});
        }
        {
            var Q0;
            Q0=makeQuery(id+"F1.opExtrude","CAP_EDGE",EDGE,{"disambiguationData":[OSD([sQuery(id+"F0.wireOp",EDGE,"E1.bottom")])],"isStart":false});
            fillet(context, id + "F15", {"entities" : qUnion([Q0]), "radius" : 2 * mm, "tangentPropagation" : true, "allowEdgeOverflow" : false});
        }
        {
            var Q0;
            {var subQ0=sQuery(id+"F0.wireOp",EDGE,"E21.filletArc");var subQ1=sQuery(id+"F0.wireOp",EDGE,"E7");var subQ2=sQuery(id+"F0.wireOp",EDGE,"E6");var subQ3=sQuery(id+"F0.wireOp",EDGE,"E5");var subQ4=sQuery(id+"F0.wireOp",EDGE,"E4");var subQ5=sQuery(id+"F0.wireOp",EDGE,"E22.filletArc");var subQ6=sQuery(id+"F0.wireOp",EDGE,"E1.bottom");var subQ7=sQuery(id+"F0.wireOp",EDGE,"E1.right");var subQ8=sQuery(id+"F0.wireOp",EDGE,"E1.top");var subQ9=sQuery(id+"F0.wireOp",EDGE,"E1.left");var subQ10=sQuery(id+"F0.wireOp",EDGE,"E23.filletArc");var subQ11=sQuery(id+"F0.wireOp",EDGE,"E24.filletArc");Q0=makeQuery(id+"F2.boolean.opBoolean","SPLIT",FACE,{"disambiguationData":[TD([makeQuery(id+"F1.opExtrude","SWEPT_FACE",FACE,{"disambiguationData":[OSD([subQ6])]})])],"derivedFrom":makeQuery(id+"F1.opExtrude","CAP_FACE",FACE,{"disambiguationData":[OSD([subQ6,subQ8,subQ9,subQ7,subQ4,subQ3,subQ2,subQ1,subQ0,subQ5,subQ10,subQ11])],"isStart":true})});}
            var sketch = newSketch(context, id + "F16", { "sketchPlane" : qUnion([Q0])});
            skLineSegment(sketch, "E79.0", {"start": v(-64.25, 74.25) * mm, "end": v(64.25, 74.25) * mm});
            skArc(sketch, "E79.1", {"start": v(-64.25, 74.25) * mm, "mid": v(-71.32, 71.32) * mm, "end": v(-74.25, 64.25) * mm});
            skLineSegment(sketch, "E79.2", {"start": v(-74.25, -64.25) * mm, "end": v(-74.25, 64.25) * mm});
            skArc(sketch, "E79.3", {"start": v(74.25, 64.25) * mm, "mid": v(71.32, 71.32) * mm, "end": v(64.25, 74.25) * mm});
            skLineSegment(sketch, "E79.4", {"start": v(74.25, -64.25) * mm, "end": v(74.25, 64.25) * mm});
            skArc(sketch, "E79.5", {"start": v(64.25, -74.25) * mm, "mid": v(71.32, -71.32) * mm, "end": v(74.25, -64.25) * mm});
            skLineSegment(sketch, "E79.6", {"start": v(-64.25, -74.25) * mm, "end": v(64.25, -74.25) * mm});
            skArc(sketch, "E79.7", {"start": v(-74.25, -64.25) * mm, "mid": v(-71.32, -71.32) * mm, "end": v(-64.25, -74.25) * mm});
            skArc(sketch, "E79.8", {"start": v(-54.26, -47.88) * mm, "mid": v(0, -60) * mm, "end": v(54.26, -47.88) * mm});
            skArc(sketch, "E79.9", {"start": v(-60, -38.83) * mm, "mid": v(-58.44, -44.2) * mm, "end": v(-54.26, -47.88) * mm});
            skLineSegment(sketch, "E79.10", {"start": v(-60, 38.83) * mm, "end": v(-60, -38.83) * mm});
            skArc(sketch, "E79.11", {"start": v(-54.26, 47.88) * mm, "mid": v(-58.44, 44.2) * mm, "end": v(-60, 38.83) * mm});
            skArc(sketch, "E79.12", {"start": v(54.26, 47.88) * mm, "mid": v(0, 60) * mm, "end": v(-54.26, 47.88) * mm});
            skLineSegment(sketch, "E79.13", {"start": v(60, 38.83) * mm, "end": v(60, -38.83) * mm});
            skArc(sketch, "E79.14", {"start": v(60, 38.83) * mm, "mid": v(58.44, 44.2) * mm, "end": v(54.26, 47.88) * mm});
            skArc(sketch, "E79.15", {"start": v(54.26, -47.88) * mm, "mid": v(58.44, -44.2) * mm, "end": v(60, -38.83) * mm});
            skCircle(sketch, "E79.16", {"center": v(-60, 60) * mm, "radius": 4 * mm});
            skCircle(sketch, "E79.17", {"center": v(60, 60) * mm, "radius": 4 * mm});
            skCircle(sketch, "E79.18", {"center": v(60, -60) * mm, "radius": 4 * mm});
            skCircle(sketch, "E79.19", {"center": v(-60, -60) * mm, "radius": 4 * mm});
            skLineSegment(sketch, "E80", {"start": v(0, 74.25) * mm, "end": v(0, 104.25) * mm, "construction": true});
            skCircle(sketch, "E81", {"center": v(0, 104.25) * mm, "radius": 6 * mm});
            skLineSegment(sketch, "E82", {"start": v(-33, 74.25) * mm, "end": v(-15, 92.25) * mm});
            skLineSegment(sketch, "E83", {"start": v(33, 74.25) * mm, "end": v(15, 92.25) * mm});
            skLineSegment(sketch, "E84", {"start": v(-15, 92.25) * mm, "end": v(-15, 104.25) * mm});
            skLineSegment(sketch, "E85", {"start": v(15, 92.25) * mm, "end": v(15, 104.25) * mm});
            skArc(sketch, "E86", {"start": v(-15, 104.25) * mm, "mid": v(0, 119.25) * mm, "end": v(15, 104.25) * mm});
            skLineSegment(sketch, "E87", {"start": v(-74.25, 0) * mm, "end": v(74.25, 0) * mm, "construction": true});
            skLineSegment(sketch, "E88.MirrorCS", {"start": v(-33, -74.25) * mm, "end": v(-15, -92.25) * mm});
            skLineSegment(sketch, "E89.MirrorCS", {"start": v(-15, -92.25) * mm, "end": v(-15, -104.25) * mm});
            skArc(sketch, "E90.MirrorCS", {"start": v(-15, -104.25) * mm, "mid": v(0, -119.25) * mm, "end": v(15, -104.25) * mm});
            skLineSegment(sketch, "E91.MirrorCS", {"start": v(15, -92.25) * mm, "end": v(15, -104.25) * mm});
            skLineSegment(sketch, "E92.MirrorCS", {"start": v(33, -74.25) * mm, "end": v(15, -92.25) * mm});
            skLineSegment(sketch, "E93.MirrorCS", {"start": v(0, -74.25) * mm, "end": v(0, -104.25) * mm, "construction": true});
            skCircle(sketch, "E94.MirrorC", {"center": v(0, -104.25) * mm, "radius": 6 * mm});
            skSolve(sketch);
        }
        {
            var Q0;
            Q0=makeQuery(id+"F16.imprint","IMPRINT",FACE,{"disambiguationData":[TD([[makeQuery(id+"F16.imprint","IMPRINT",EDGE,{"derivedFrom":sQuery(id+"F16.wireOp",EDGE,"E81")}),-1.0]])]});
            var Q1;
            Q1 = qSketchRegion(id + "F16", true);
            var Q2;
            Q2=makeQuery(id+"F2.opExtrude","CAP_FACE",FACE,{"disambiguationData":[OSD([sQuery(id+"F0.wireOp",EDGE,"E12"),sQuery(id+"F0.wireOp",EDGE,"E13"),sQuery(id+"F0.wireOp",EDGE,"E14"),sQuery(id+"F0.wireOp",EDGE,"E15"),sQuery(id+"F0.wireOp",EDGE,"E17.filletArc"),sQuery(id+"F0.wireOp",EDGE,"E18.filletArc"),sQuery(id+"F0.wireOp",EDGE,"E19.filletArc"),sQuery(id+"F0.wireOp",EDGE,"E20.filletArc"),sQuery(id+"F0.wireOp",EDGE,"E25.0"),sQuery(id+"F0.wireOp",EDGE,"E25.1"),sQuery(id+"F0.wireOp",EDGE,"E25.2"),sQuery(id+"F0.wireOp",EDGE,"E25.3"),sQuery(id+"F0.wireOp",EDGE,"E25.4"),sQuery(id+"F0.wireOp",EDGE,"E25.5"),sQuery(id+"F0.wireOp",EDGE,"E25.6"),sQuery(id+"F0.wireOp",EDGE,"E25.7")])],"isStart":false});
            extrude(context, id + "F17", {"entities" : qUnion([Q0, Q1]), "endBound" : BoundingType.UP_TO_SURFACE, "depth" : 25 * mm, "endBoundEntityFace" : qUnion([Q2]), "offsetDistance" : 25 * mm});
        }
    });
